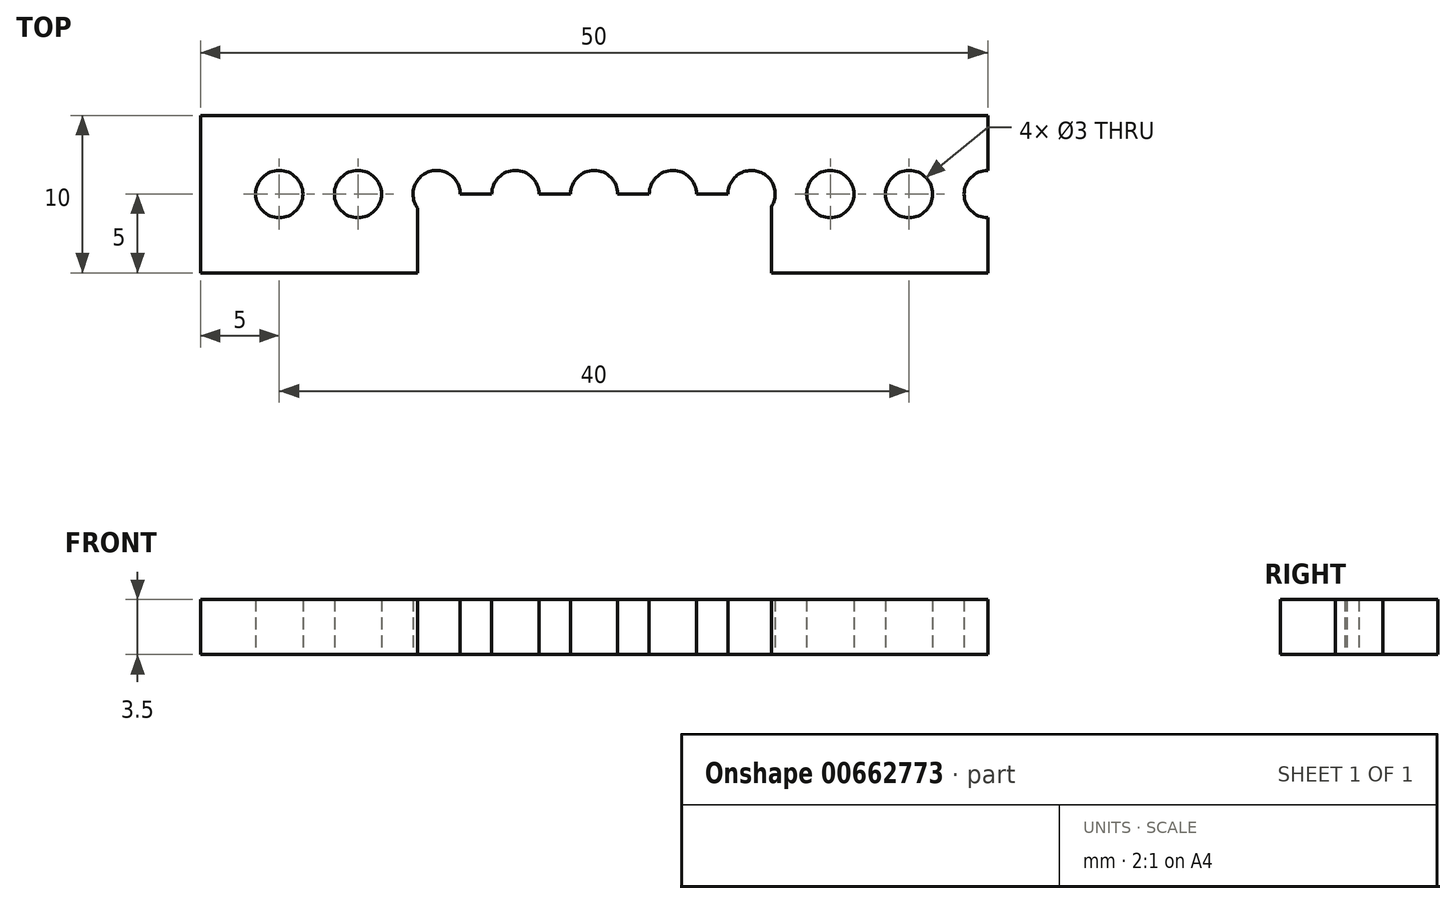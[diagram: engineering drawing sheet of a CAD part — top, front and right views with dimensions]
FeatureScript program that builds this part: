
annotation { "Feature Type Name" : "Feature", "Feature Type Description" : "" }
export const myFeature = defineFeature(function(context is Context, id is Id, definition is map)
    precondition{}
    {
        {
            var Q0;
            Q0=qCreatedBy(makeId("Top.planeOp"),FACE);
            var sketch = newSketch(context, id + "F0", { "sketchPlane" : qUnion([Q0])});
            skLineSegment(sketch, "E0.bottom", {"start": v(25, -5) * mm, "end": v(-25, -5) * mm});
            skLineSegment(sketch, "E0.top", {"start": v(25, 5) * mm, "end": v(-25, 5) * mm});
            skLineSegment(sketch, "E0.left", {"start": v(25, -5) * mm, "end": v(25, 5) * mm});
            skLineSegment(sketch, "E0.right", {"start": v(-25, -5) * mm, "end": v(-25, 5) * mm});
            skPoint(sketch, "E0.middle", {"position": v(0, 0) * mm});
            skLineSegment(sketch, "E1", {"start": v(-25, 0) * mm, "end": v(-20, 0) * mm, "construction": true});
            skCircle(sketch, "E2", {"center": v(-20, 0) * mm, "radius": 1.5 * mm});
            skCircle(sketch, "E3.1.0.0", {"center": v(-15, 0) * mm, "radius": 1.5 * mm});
            skCircle(sketch, "E3.2.0.0", {"center": v(-10, 0) * mm, "radius": 1.5 * mm});
            skCircle(sketch, "E3.3.0.0", {"center": v(-5, 0) * mm, "radius": 1.5 * mm});
            skCircle(sketch, "E3.4.0.0", {"center": v(0, 0) * mm, "radius": 1.5 * mm});
            skCircle(sketch, "E3.5.0.0", {"center": v(5, 0) * mm, "radius": 1.5 * mm});
            skLineSegment(sketch, "E3.direction1", {"start": v(-20, 0) * mm, "end": v(-15, 0) * mm, "construction": true});
            skCircle(sketch, "E4.0.6.0", {"center": v(10, 0) * mm, "radius": 1.5 * mm});
            skCircle(sketch, "E4.0.7.0", {"center": v(15, 0) * mm, "radius": 1.5 * mm});
            skCircle(sketch, "E5.0.8.0", {"center": v(20, 0) * mm, "radius": 1.5 * mm});
            skCircle(sketch, "E5.0.9.0", {"center": v(25, 0) * mm, "radius": 1.5 * mm});
            skSolve(sketch);
        }
        {
            var Q0;
            Q0=makeQuery(id+"F0.imprint","IMPRINT",FACE,{"disambiguationData":[TD([[makeQuery(id+"F0.imprint","IMPRINT",EDGE,{"derivedFrom":sQuery(id+"F0.wireOp",EDGE,"E0.bottom")}),-1.0]])]});
            extrude(context, id + "F1", {"entities" : qUnion([Q0]), "depth" : 3.5 * mm, "offsetDistance" : 25 * mm});
        }
        {
            var Q0;
            Q0=makeQuery(id+"F1.opExtrude","SWEPT_FACE",FACE,{"disambiguationData":[OSD([sQuery(id+"F0.wireOp",EDGE,"E0.bottom")])]});
            var sketch = newSketch(context, id + "F2", { "sketchPlane" : qUnion([Q0])});
            skLineSegment(sketch, "E6.bottom", {"start": v(-11.2, 3.5) * mm, "end": v(11.28, 3.5) * mm});
            skLineSegment(sketch, "E6.top", {"start": v(-11.2, 0) * mm, "end": v(11.28, 0) * mm});
            skLineSegment(sketch, "E6.left", {"start": v(-11.2, 3.5) * mm, "end": v(-11.2, 0) * mm});
            skLineSegment(sketch, "E6.right", {"start": v(11.28, 3.5) * mm, "end": v(11.28, 0) * mm});
            skLineSegment(sketch, "E7", {"start": v(-11.2, 0) * mm, "end": v(-25, 0) * mm, "construction": true});
            skSolve(sketch);
        }
        {
            var Q0;
            Q0=makeQuery(id+"F2.imprint","IMPRINT",FACE,{"disambiguationData":[TD([[makeQuery(id+"F2.imprint","IMPRINT",EDGE,{"derivedFrom":sQuery(id+"F2.wireOp",EDGE,"E6.bottom")}),1.0]])]});
            extrude(context, id + "F3", {"entities" : qUnion([Q0]), "operationType" : NewBodyOperationType.REMOVE, "oppositeDirection" : true, "depth" : 5 * mm, "offsetDistance" : 25 * mm});
        }
    });
